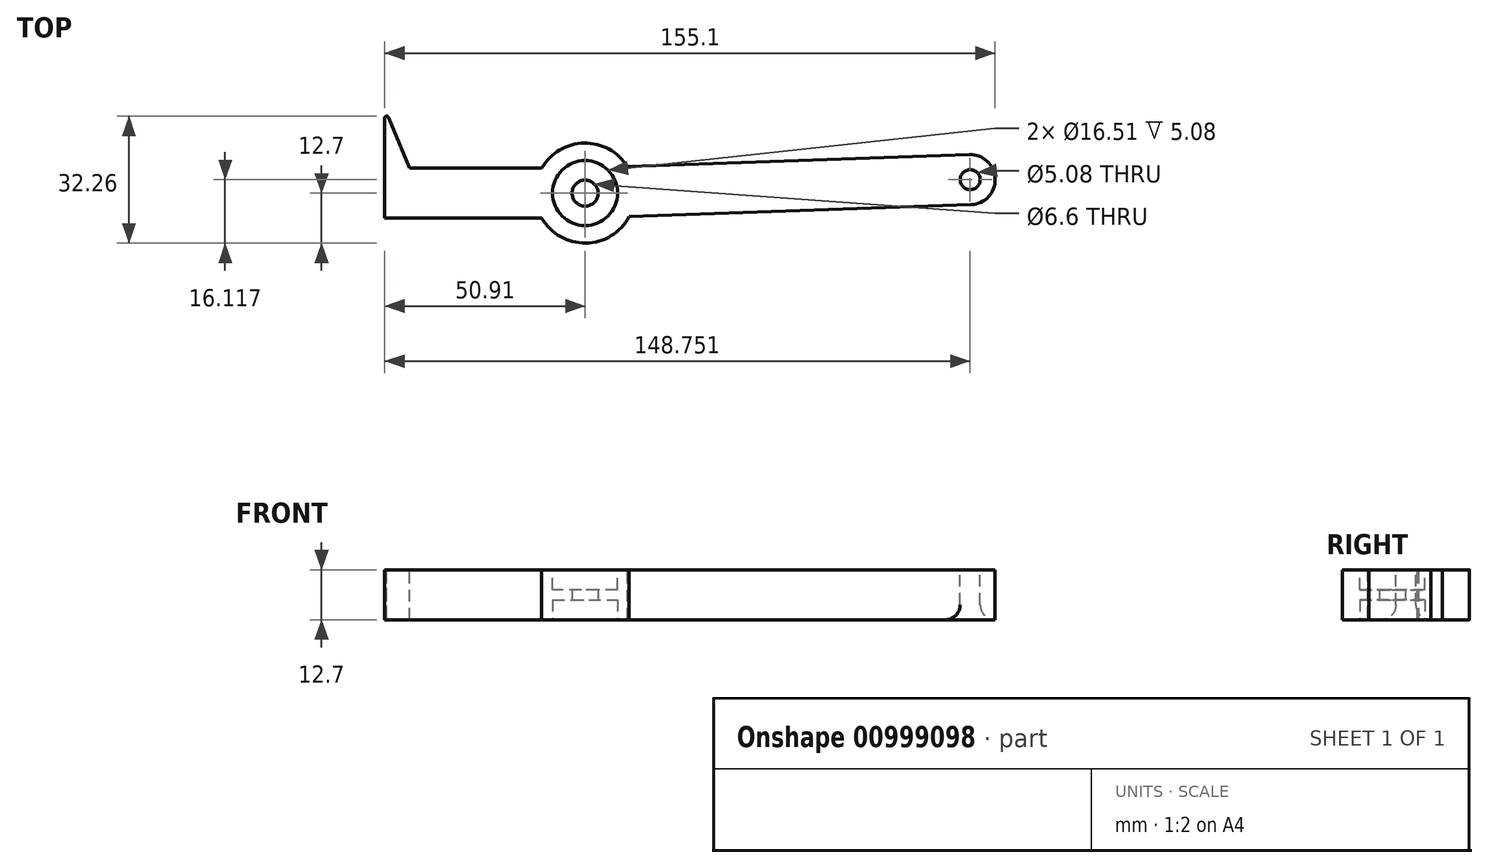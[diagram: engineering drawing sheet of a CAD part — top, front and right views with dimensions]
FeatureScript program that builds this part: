
annotation { "Feature Type Name" : "Feature", "Feature Type Description" : "" }
export const myFeature = defineFeature(function(context is Context, id is Id, definition is map)
    precondition{}
    {
        {
            var Q0;
            Q0=qCreatedBy(makeId("Top.planeOp"),FACE);
            var sketch = newSketch(context, id + "F0", { "sketchPlane" : qUnion([Q0])});
            skLineSegment(sketch, "E0.bottom", {"start": v(-50.91, 6.35) * mm, "end": v(-0.11, 6.35) * mm});
            skLineSegment(sketch, "E0.top", {"start": v(-50.91, -6.35) * mm, "end": v(0.11, -6.35) * mm});
            skLineSegment(sketch, "E0.left", {"start": v(-50.91, 6.35) * mm, "end": v(-50.91, -6.35) * mm});
            skLineSegment(sketch, "E1", {"start": v(0, 0) * mm, "end": v(-50.91, 0) * mm, "construction": true});
            skCircle(sketch, "E2", {"center": v(0, 0) * mm, "radius": 5.08 * mm, "construction": true});
            skLineSegment(sketch, "E3", {"start": v(0.11, -6.35) * mm, "end": v(104.4, -2.7) * mm});
            skLineSegment(sketch, "E4", {"start": v(104.4, -2.7) * mm, "end": v(103.97, 9.98) * mm});
            skLineSegment(sketch, "E5", {"start": v(103.97, 9.98) * mm, "end": v(-0.11, 6.35) * mm});
            skLineSegment(sketch, "E6", {"start": v(0.11, -6.35) * mm, "end": v(0, 0) * mm, "construction": true});
            skLineSegment(sketch, "E7", {"start": v(-0.11, 6.35) * mm, "end": v(0, 0) * mm, "construction": true});
            skSolve(sketch);
        }
        {
            var Q0;
            Q0 = qSketchRegion(id + "F0", true);
            extrude(context, id + "F1", {"entities" : qUnion([Q0]), "depth" : 12.7 * mm, "offsetDistance" : 25.4 * mm});
        }
        {
            var Q0;
            Q0=makeQuery(id+"F1.opExtrude","CAP_FACE",FACE,{"disambiguationData":[OSD([sQuery(id+"F0.wireOp",EDGE,"E0.bottom"),sQuery(id+"F0.wireOp",EDGE,"E0.top"),sQuery(id+"F0.wireOp",EDGE,"E0.left"),sQuery(id+"F0.wireOp",EDGE,"E0.right"),sQuery(id+"F0.wireOp",EDGE,"E2")])],"isStart":false});
            var sketch = newSketch(context, id + "F2", { "sketchPlane" : qUnion([Q0])});
            skLineSegment(sketch, "E8", {"start": v(-50.91, 6.35) * mm, "end": v(-50.91, 21.59) * mm});
            skLineSegment(sketch, "E9", {"start": v(-50.91, 21.59) * mm, "end": v(-44.56, 6.35) * mm});
            skLineSegment(sketch, "E10", {"start": v(-44.56, 6.35) * mm, "end": v(-50.91, 6.35) * mm});
            skSolve(sketch);
        }
        {
            var Q0;
            Q0 = qSketchRegion(id + "F2", true);
            var Q1;
            Q1=makeQuery(id+"F1.opExtrude","CAP_FACE",FACE,{"disambiguationData":[OSD([sQuery(id+"F0.wireOp",EDGE,"E0.bottom"),sQuery(id+"F0.wireOp",EDGE,"E0.top"),sQuery(id+"F0.wireOp",EDGE,"E0.left"),sQuery(id+"F0.wireOp",EDGE,"E0.right"),sQuery(id+"F0.wireOp",EDGE,"E2")])],"isStart":true});
            extrude(context, id + "F3", {"entities" : qUnion([Q0]), "operationType" : NewBodyOperationType.ADD, "endBound" : BoundingType.UP_TO_SURFACE, "oppositeDirection" : true, "depth" : 25.4 * mm, "endBoundEntityFace" : qUnion([Q1]), "offsetDistance" : 25.4 * mm});
        }
        {
            var Q0;
            Q0=makeQuery(id+"F3.boolean.opBoolean","MERGE",FACE,{"derivedFrom":[makeQuery(id+"F1.opExtrude","CAP_FACE",FACE,{"disambiguationData":[OSD([sQuery(id+"F0.wireOp",EDGE,"E0.bottom"),sQuery(id+"F0.wireOp",EDGE,"E0.top"),sQuery(id+"F0.wireOp",EDGE,"E0.left"),sQuery(id+"F0.wireOp",EDGE,"E2"),sQuery(id+"F0.wireOp",EDGE,"E3"),sQuery(id+"F0.wireOp",EDGE,"E4"),sQuery(id+"F0.wireOp",EDGE,"E5")])],"isStart":false}),makeQuery(id+"F3.opExtrude","CAP_FACE",FACE,{"disambiguationData":[OSD([sQuery(id+"F2.wireOp",EDGE,"E8"),sQuery(id+"F2.wireOp",EDGE,"E9"),sQuery(id+"F2.wireOp",EDGE,"E10")])],"isStart":true})]});
            var sketch = newSketch(context, id + "F4", { "sketchPlane" : qUnion([Q0])});
            skCircle(sketch, "E11", {"center": v(97.84, 3.42) * mm, "radius": 2.54 * mm});
            skLineSegment(sketch, "E12", {"start": v(97.84, 3.42) * mm, "end": v(97.62, 9.76) * mm, "construction": true});
            skLineSegment(sketch, "E13", {"start": v(97.84, 3.42) * mm, "end": v(98.06, -2.93) * mm, "construction": true});
            skSolve(sketch);
        }
        {
            var Q0;
            Q0 = qSketchRegion(id + "F4", true);
            extrude(context, id + "F5", {"entities" : qUnion([Q0]), "operationType" : NewBodyOperationType.REMOVE, "endBound" : BoundingType.THROUGH_ALL, "oppositeDirection" : true, "depth" : 25.4 * mm, "offsetDistance" : 25.4 * mm});
        }
        {
            var Q0;
            Q0=makeQuery(id+"F1.opExtrude","SWEPT_EDGE",EDGE,{"disambiguationData":[OSD([sQuery(id+"F0.wireOp",EDGE,"E4"),sQuery(id+"F0.wireOp",EDGE,"E5")])]});
            var Q1;
            Q1=makeQuery(id+"F1.opExtrude","SWEPT_EDGE",EDGE,{"disambiguationData":[OSD([sQuery(id+"F0.wireOp",EDGE,"E3"),sQuery(id+"F0.wireOp",EDGE,"E4")])]});
            fillet(context, id + "F6", {"entities" : qUnion([Q0, Q1]), "radius" : 6.35 * mm, "tangentPropagation" : true, "allowEdgeOverflow" : false});
        }
        {
            var Q0;
            Q0=makeQuery(id+"F1.opExtrude","SWEPT_EDGE",EDGE,{"disambiguationData":[OSD([sQuery(id+"F0.wireOp",EDGE,"E0.top"),sQuery(id+"F0.wireOp",EDGE,"E3")])]});
            fillet(context, id + "F7", {"entities" : qUnion([Q0]), "radius" : 12.7 * mm, "tangentPropagation" : true, "allowEdgeOverflow" : false});
        }
        {
            var Q0;
            Q0=makeQuery(id+"F3.boolean.opBoolean","MERGE",FACE,{"derivedFrom":[makeQuery(id+"F1.opExtrude","CAP_FACE",FACE,{"disambiguationData":[OSD([sQuery(id+"F0.wireOp",EDGE,"E0.bottom"),sQuery(id+"F0.wireOp",EDGE,"E0.top"),sQuery(id+"F0.wireOp",EDGE,"E0.left"),sQuery(id+"F0.wireOp",EDGE,"E2"),sQuery(id+"F0.wireOp",EDGE,"E3"),sQuery(id+"F0.wireOp",EDGE,"E4"),sQuery(id+"F0.wireOp",EDGE,"E5")])],"isStart":false}),makeQuery(id+"F3.opExtrude","CAP_FACE",FACE,{"disambiguationData":[OSD([sQuery(id+"F2.wireOp",EDGE,"E8"),sQuery(id+"F2.wireOp",EDGE,"E9"),sQuery(id+"F2.wireOp",EDGE,"E10")])],"isStart":true})]});
            var sketch = newSketch(context, id + "F8", { "sketchPlane" : qUnion([Q0])});
            skCircle(sketch, "E14", {"center": v(0, 0) * mm, "radius": 12.7 * mm});
            skSolve(sketch);
        }
        {
            var Q0;
            Q0 = qSketchRegion(id + "F8", true);
            var Q1;
            Q1=makeQuery(id+"F3.boolean.opBoolean","MERGE",FACE,{"derivedFrom":[makeQuery(id+"F1.opExtrude","CAP_FACE",FACE,{"disambiguationData":[OSD([sQuery(id+"F0.wireOp",EDGE,"E0.bottom"),sQuery(id+"F0.wireOp",EDGE,"E0.top"),sQuery(id+"F0.wireOp",EDGE,"E0.left"),sQuery(id+"F0.wireOp",EDGE,"E2"),sQuery(id+"F0.wireOp",EDGE,"E3"),sQuery(id+"F0.wireOp",EDGE,"E4"),sQuery(id+"F0.wireOp",EDGE,"E5")])],"isStart":true}),makeQuery(id+"F3.opExtrude","CAP_FACE",FACE,{"disambiguationData":[OSD([sQuery(id+"F2.wireOp",EDGE,"E8"),sQuery(id+"F2.wireOp",EDGE,"E9"),sQuery(id+"F2.wireOp",EDGE,"E10")])],"isStart":false})]});
            extrude(context, id + "F9", {"entities" : qUnion([Q0]), "operationType" : NewBodyOperationType.ADD, "endBound" : BoundingType.UP_TO_SURFACE, "oppositeDirection" : true, "depth" : 25.4 * mm, "endBoundEntityFace" : qUnion([Q1]), "offsetDistance" : 25.4 * mm});
        }
        {
            var Q0;
            Q0=makeQuery(id+"F9.boolean.opBoolean","MERGE",FACE,{"derivedFrom":[makeQuery(id+"F3.boolean.opBoolean","MERGE",FACE,{"derivedFrom":[makeQuery(id+"F1.opExtrude","CAP_FACE",FACE,{"disambiguationData":[OSD([sQuery(id+"F0.wireOp",EDGE,"E0.bottom"),sQuery(id+"F0.wireOp",EDGE,"E0.top"),sQuery(id+"F0.wireOp",EDGE,"E0.left"),sQuery(id+"F0.wireOp",EDGE,"E2"),sQuery(id+"F0.wireOp",EDGE,"E3"),sQuery(id+"F0.wireOp",EDGE,"E4"),sQuery(id+"F0.wireOp",EDGE,"E5")])],"isStart":true}),makeQuery(id+"F3.opExtrude","CAP_FACE",FACE,{"disambiguationData":[OSD([sQuery(id+"F2.wireOp",EDGE,"E8"),sQuery(id+"F2.wireOp",EDGE,"E9"),sQuery(id+"F2.wireOp",EDGE,"E10")])],"isStart":false})]}),makeQuery(id+"F9.opExtrude","CAP_FACE",FACE,{"disambiguationData":[OSD([sQuery(id+"F8.wireOp",EDGE,"d8a4dec7-a91a-4df0-a0c1-9e269386a2b0"),sQuery(id+"F8.wireOp",EDGE,"xE5WhkZk-Re9x-Y3ce-ES6c-HCC58elwfYPf"),sQuery(id+"F8.wireOp",EDGE,"dOoWU5O4-qePF-9RIY-oP5g-ppaTESg4B05Y")])],"isStart":false})]});
            var sketch = newSketch(context, id + "F10", { "sketchPlane" : qUnion([Q0])});
            skCircle(sketch, "E15", {"center": v(0, 0) * mm, "radius": 8.26 * mm});
            skSolve(sketch);
        }
        {
            var Q0;
            Q0 = qSketchRegion(id + "F10", true);
            extrude(context, id + "F11", {"entities" : qUnion([Q0]), "operationType" : NewBodyOperationType.REMOVE, "oppositeDirection" : true, "depth" : 5.08 * mm, "offsetDistance" : 25.4 * mm});
        }
        {
            var Q0;
            Q0=makeQuery(id+"F9.boolean.opBoolean","MERGE",FACE,{"derivedFrom":[makeQuery(id+"F3.boolean.opBoolean","MERGE",FACE,{"derivedFrom":[makeQuery(id+"F1.opExtrude","CAP_FACE",FACE,{"disambiguationData":[OSD([sQuery(id+"F0.wireOp",EDGE,"E0.bottom"),sQuery(id+"F0.wireOp",EDGE,"E0.top"),sQuery(id+"F0.wireOp",EDGE,"E0.left"),sQuery(id+"F0.wireOp",EDGE,"E2"),sQuery(id+"F0.wireOp",EDGE,"E3"),sQuery(id+"F0.wireOp",EDGE,"E4"),sQuery(id+"F0.wireOp",EDGE,"E5")])],"isStart":false}),makeQuery(id+"F3.opExtrude","CAP_FACE",FACE,{"disambiguationData":[OSD([sQuery(id+"F2.wireOp",EDGE,"E8"),sQuery(id+"F2.wireOp",EDGE,"E9"),sQuery(id+"F2.wireOp",EDGE,"E10")])],"isStart":true})]}),makeQuery(id+"F9.opExtrude","CAP_FACE",FACE,{"disambiguationData":[OSD([sQuery(id+"F8.wireOp",EDGE,"d8a4dec7-a91a-4df0-a0c1-9e269386a2b0"),sQuery(id+"F8.wireOp",EDGE,"xE5WhkZk-Re9x-Y3ce-ES6c-HCC58elwfYPf"),sQuery(id+"F8.wireOp",EDGE,"dOoWU5O4-qePF-9RIY-oP5g-ppaTESg4B05Y")])],"isStart":true})]});
            var sketch = newSketch(context, id + "F12", { "sketchPlane" : qUnion([Q0])});
            skCircle(sketch, "E16", {"center": v(0, 0) * mm, "radius": 8.26 * mm});
            skSolve(sketch);
        }
        {
            var Q0;
            Q0 = qSketchRegion(id + "F12", true);
            extrude(context, id + "F13", {"entities" : qUnion([Q0]), "operationType" : NewBodyOperationType.REMOVE, "oppositeDirection" : true, "depth" : 5.08 * mm, "offsetDistance" : 25.4 * mm});
        }
        {
            var Q0;
            Q0=makeQuery(id+"F3.opExtrude","SWEPT_EDGE",EDGE,{"disambiguationData":[OSD([sQuery(id+"F2.wireOp",EDGE,"E8"),sQuery(id+"F2.wireOp",EDGE,"E9")])]});
            fillet(context, id + "F14", {"entities" : qUnion([Q0]), "radius" : 0.5 * mm, "tangentPropagation" : true, "allowEdgeOverflow" : false});
        }
        {
            var Q0;
            Q0=makeQuery(id+"F9.boolean.opBoolean","MERGE",FACE,{"derivedFrom":[makeQuery(id+"F3.boolean.opBoolean","MERGE",FACE,{"derivedFrom":[makeQuery(id+"F1.opExtrude","CAP_FACE",FACE,{"disambiguationData":[OSD([sQuery(id+"F0.wireOp",EDGE,"E0.bottom"),sQuery(id+"F0.wireOp",EDGE,"E0.top"),sQuery(id+"F0.wireOp",EDGE,"E0.left"),sQuery(id+"F0.wireOp",EDGE,"E2"),sQuery(id+"F0.wireOp",EDGE,"E3"),sQuery(id+"F0.wireOp",EDGE,"E4"),sQuery(id+"F0.wireOp",EDGE,"E5")])],"isStart":false}),makeQuery(id+"F3.opExtrude","CAP_FACE",FACE,{"disambiguationData":[OSD([sQuery(id+"F2.wireOp",EDGE,"E8"),sQuery(id+"F2.wireOp",EDGE,"E9"),sQuery(id+"F2.wireOp",EDGE,"E10")])],"isStart":true})]}),makeQuery(id+"F9.opExtrude","CAP_FACE",FACE,{"disambiguationData":[OSD([sQuery(id+"F8.wireOp",EDGE,"d8a4dec7-a91a-4df0-a0c1-9e269386a2b0"),sQuery(id+"F8.wireOp",EDGE,"xE5WhkZk-Re9x-Y3ce-ES6c-HCC58elwfYPf"),sQuery(id+"F8.wireOp",EDGE,"dOoWU5O4-qePF-9RIY-oP5g-ppaTESg4B05Y")])],"isStart":true})]});
            var sketch = newSketch(context, id + "F15", { "sketchPlane" : qUnion([Q0])});
            skLineSegment(sketch, "E17", {"start": v(-50.53, 19.54) * mm, "end": v(-50.4, 19.05) * mm, "construction": true});
            skLineSegment(sketch, "E18", {"start": v(-50.53, 19.54) * mm, "end": v(-50.48, 19.55) * mm});
            skLineSegment(sketch, "E19", {"start": v(-50.48, 19.55) * mm, "end": v(-50.4, 19.05) * mm, "construction": true});
            skLineSegment(sketch, "E20", {"start": v(-50.4, 19.05) * mm, "end": v(-50.5, 19.55) * mm, "construction": true});
            skLineSegment(sketch, "E21", {"start": v(-49.93, 19.25) * mm, "end": v(-50.91, 19.05) * mm, "construction": true});
            skLineSegment(sketch, "E22", {"start": v(-50.48, 19.55) * mm, "end": v(-50.5, 19.5) * mm});
            skLineSegment(sketch, "E23", {"start": v(-50.5, 19.5) * mm, "end": v(-50.53, 19.54) * mm});
            skSolve(sketch);
        }
        {
            var Q0;
            Q0 = qSketchRegion(id + "F15", true);
            extrude(context, id + "F16", {"entities" : qUnion([Q0]), "operationType" : NewBodyOperationType.REMOVE, "endBound" : BoundingType.THROUGH_ALL, "oppositeDirection" : true, "depth" : 25.4 * mm, "offsetDistance" : 25.4 * mm});
        }
        {
            var Q0;
            Q0=makeQuery(id+"F11.boolean.opBoolean","COPY",FACE,{"derivedFrom":makeQuery(id+"F11.opExtrude","CAP_FACE",FACE,{"disambiguationData":[OSD([sQuery(id+"F10.wireOp",EDGE,"E15")])],"isStart":false})});
            var sketch = newSketch(context, id + "F17", { "sketchPlane" : qUnion([Q0])});
            skCircle(sketch, "E24", {"center": v(0, 0) * mm, "radius": 3.3 * mm});
            skSolve(sketch);
        }
        {
            var Q0;
            Q0 = qSketchRegion(id + "F17", true);
            extrude(context, id + "F18", {"entities" : qUnion([Q0]), "operationType" : NewBodyOperationType.REMOVE, "endBound" : BoundingType.THROUGH_ALL, "oppositeDirection" : true, "depth" : 25.4 * mm, "offsetDistance" : 25.4 * mm});
        }
        {
            var Q0;
            Q0=makeQuery(id+"F5.boolean.opBoolean","COPY",EDGE,{"derivedFrom":makeQuery(id+"F5.opExtrude","CAP_EDGE",EDGE,{"disambiguationData":[OSD([sQuery(id+"F4.wireOp",EDGE,"E11")])],"isStart":true})});
            var Q1;
            Q1=makeQuery(id+"F5.boolean.opBoolean","INTERSECT",EDGE,{"derivedFrom":[makeQuery(id+"F3.boolean.opBoolean","MERGE",FACE,{"derivedFrom":[makeQuery(id+"F1.opExtrude","CAP_FACE",FACE,{"disambiguationData":[OSD([sQuery(id+"F0.wireOp",EDGE,"E0.bottom"),sQuery(id+"F0.wireOp",EDGE,"E0.top"),sQuery(id+"F0.wireOp",EDGE,"E0.left"),sQuery(id+"F0.wireOp",EDGE,"E3"),sQuery(id+"F0.wireOp",EDGE,"E4"),sQuery(id+"F0.wireOp",EDGE,"E5")])],"isStart":true}),makeQuery(id+"F3.opExtrude","CAP_FACE",FACE,{"disambiguationData":[OSD([sQuery(id+"F2.wireOp",EDGE,"E8"),sQuery(id+"F2.wireOp",EDGE,"E9"),sQuery(id+"F2.wireOp",EDGE,"E10")])],"isStart":false})]}),makeQuery(id+"F5.opExtrude","SWEPT_FACE",FACE,{"disambiguationData":[OSD([sQuery(id+"F4.wireOp",EDGE,"E11")])]})]});
            fillet(context, id + "F19", {"entities" : qUnion([Q0, Q1]), "radius" : 3.8 * mm, "tangentPropagation" : true, "allowEdgeOverflow" : false});
        }
    });
